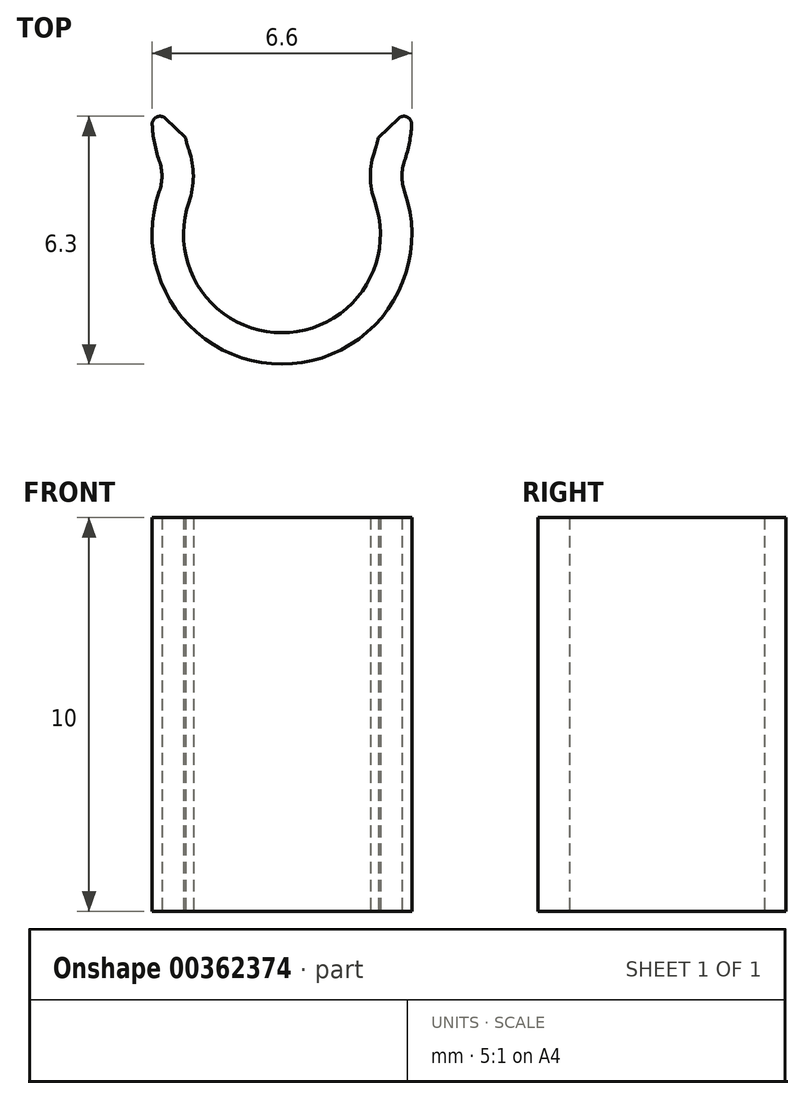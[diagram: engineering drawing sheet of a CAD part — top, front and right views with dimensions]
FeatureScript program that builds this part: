
annotation { "Feature Type Name" : "Feature", "Feature Type Description" : "" }
export const myFeature = defineFeature(function(context is Context, id is Id, definition is map)
    precondition{}
    {
        {
            var Q0;
            Q0=qCreatedBy(makeId("Top.planeOp"),FACE);
            var sketch = newSketch(context, id + "F0", { "sketchPlane" : qUnion([Q0])});
            skArc(sketch, "E0", {"start": v(-2.36, 0.82) * mm, "mid": v(0, -2.5) * mm, "end": v(2.36, 0.82) * mm});
            skArc(sketch, "E1", {"start": v(2.36, 2.14) * mm, "mid": v(2.41, 2.3) * mm, "end": v(2.45, 2.46) * mm});
            skPoint(sketch, "E2.visualSharp", {"position": v(-2.02, 1.48) * mm});
            skArc(sketch, "E2.filletArc", {"start": v(-2.36, 0.82) * mm, "mid": v(-2.25, 1.48) * mm, "end": v(-2.36, 2.14) * mm});
            skPoint(sketch, "E3.visualSharp", {"position": v(2.02, 1.48) * mm});
            skArc(sketch, "E3.filletArc", {"start": v(2.36, 2.14) * mm, "mid": v(2.25, 1.48) * mm, "end": v(2.36, 0.82) * mm});
            skLineSegment(sketch, "E4", {"start": v(-2.45, 2.46) * mm, "end": v(2.45, 2.46) * mm, "construction": true});
            skPoint(sketch, "E5", {"position": v(0, 2.46) * mm});
            skPoint(sketch, "E6", {"position": v(-2.45, 2.46) * mm});
            skPoint(sketch, "E7", {"position": v(2.45, 2.46) * mm});
            skArc(sketch, "E8.trimOffspring", {"start": v(-2.45, 2.46) * mm, "mid": v(-2.41, 2.3) * mm, "end": v(-2.36, 2.14) * mm});
            skPoint(sketch, "E9.orphan", {"position": v(3.3, 2.46) * mm});
            skPoint(sketch, "E10.orphan", {"position": v(-3.3, 2.46) * mm});
            skArc(sketch, "E11.0", {"start": v(-3.3, 2.79) * mm, "mid": v(-3.24, 2.32) * mm, "end": v(-3.12, 1.87) * mm});
            skArc(sketch, "E11.1", {"start": v(3.12, 1.87) * mm, "mid": v(3.24, 2.32) * mm, "end": v(3.3, 2.79) * mm});
            skArc(sketch, "E11.2", {"start": v(3.12, 1.87) * mm, "mid": v(3.05, 1.48) * mm, "end": v(3.12, 1.08) * mm});
            skLineSegment(sketch, "E11.3", {"start": v(-3.29, 3.26) * mm, "end": v(3.29, 3.26) * mm, "construction": true});
            skArc(sketch, "E11.4", {"start": v(-3.12, 1.08) * mm, "mid": v(0, -3.3) * mm, "end": v(3.12, 1.08) * mm});
            skArc(sketch, "E11.5", {"start": v(-3.12, 1.08) * mm, "mid": v(-3.05, 1.48) * mm, "end": v(-3.12, 1.87) * mm});
            skLineSegment(sketch, "E12", {"start": v(-2.45, 2.46) * mm, "end": v(-2.96, 2.94) * mm});
            skLineSegment(sketch, "E13", {"start": v(2.45, 2.46) * mm, "end": v(2.96, 2.94) * mm});
            skPoint(sketch, "E14.visualSharp", {"position": v(-3.29, 3.26) * mm});
            skArc(sketch, "E14.filletArc", {"start": v(-2.96, 2.94) * mm, "mid": v(-3.18, 2.98) * mm, "end": v(-3.3, 2.79) * mm});
            skPoint(sketch, "E15.visualSharp", {"position": v(3.29, 3.26) * mm});
            skArc(sketch, "E15.filletArc", {"start": v(3.3, 2.79) * mm, "mid": v(3.18, 2.98) * mm, "end": v(2.96, 2.94) * mm});
            skSolve(sketch);
        }
        {
            var Q0;
            Q0=makeQuery(id+"F0.imprint","IMPRINT",FACE,{"disambiguationData":[TD([[makeQuery(id+"F0.imprint","IMPRINT",EDGE,{"derivedFrom":sQuery(id+"F0.wireOp",EDGE,"E0")}),-1.0]])]});
            var Q1;
            {var subQ5=sQuery(id+"F0.wireOp",EDGE,"0tawDMtT-U5fF-7YwG-ekcF-jH6XnWLQgyGC.bottom");Q1=makeQuery(id+"F0.imprint","IMPRINT",FACE,{"disambiguationData":[TD([[makeQuery(id+"F0.imprint","IMPRINT",EDGE,{"derivedFrom":subQ5}),1.0]])]});}
            extrude(context, id + "F1", {"entities" : qUnion([Q0, Q1]), "depth" : 10 * mm});
        }
    });
